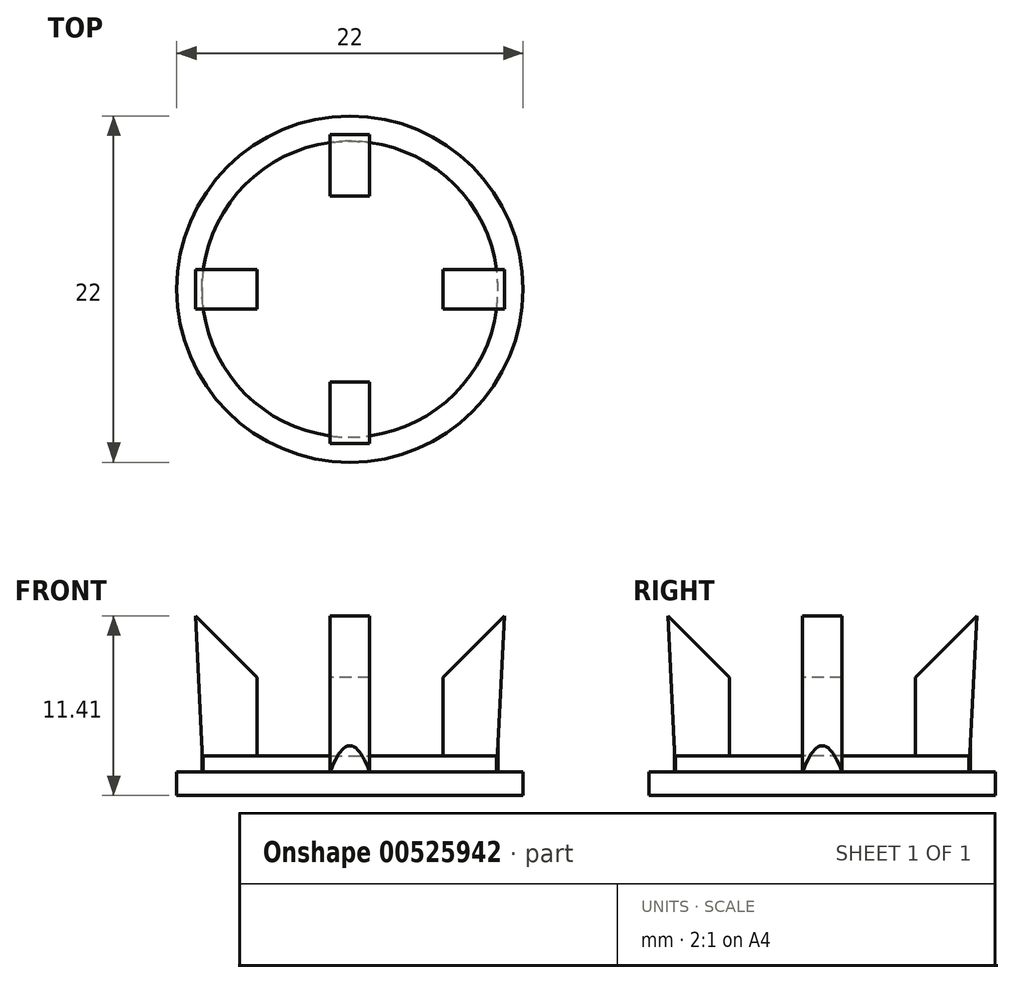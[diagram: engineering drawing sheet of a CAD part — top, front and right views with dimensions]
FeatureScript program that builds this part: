
annotation { "Feature Type Name" : "Feature", "Feature Type Description" : "" }
export const myFeature = defineFeature(function(context is Context, id is Id, definition is map)
    precondition{}
    {
        {
            var Q0;
            Q0=qCreatedBy(makeId("Top.planeOp"),FACE);
            var sketch = newSketch(context, id + "F0", { "sketchPlane" : qUnion([Q0])});
            skCircle(sketch, "E0", {"center": v(0, 0) * mm, "radius": 11 * mm});
            skCircle(sketch, "E1", {"center": v(0, 0) * mm, "radius": 9.4 * mm});
            skLineSegment(sketch, "E2.bottom", {"start": v(-12.9, 1.25) * mm, "end": v(-5.9, 1.25) * mm});
            skLineSegment(sketch, "E2.top", {"start": v(-12.9, -1.25) * mm, "end": v(-5.9, -1.25) * mm});
            skLineSegment(sketch, "E2.left", {"start": v(-12.9, 1.25) * mm, "end": v(-12.9, -1.25) * mm});
            skLineSegment(sketch, "E2.right", {"start": v(-5.9, 1.25) * mm, "end": v(-5.9, -1.25) * mm});
            skPoint(sketch, "E2.middle", {"position": v(-9.4, 0) * mm});
            skLineSegment(sketch, "E3.bottom", {"start": v(-1.25, 12.9) * mm, "end": v(1.25, 12.9) * mm});
            skLineSegment(sketch, "E3.top", {"start": v(-1.25, 5.9) * mm, "end": v(1.25, 5.9) * mm});
            skLineSegment(sketch, "E3.left", {"start": v(-1.25, 12.9) * mm, "end": v(-1.25, 5.9) * mm});
            skLineSegment(sketch, "E3.right", {"start": v(1.25, 12.9) * mm, "end": v(1.25, 5.9) * mm});
            skPoint(sketch, "E3.middle", {"position": v(0, 9.4) * mm});
            skLineSegment(sketch, "E4.bottom", {"start": v(12.9, 1.25) * mm, "end": v(5.9, 1.25) * mm});
            skLineSegment(sketch, "E4.top", {"start": v(12.9, -1.25) * mm, "end": v(5.9, -1.25) * mm});
            skLineSegment(sketch, "E4.left", {"start": v(12.9, 1.25) * mm, "end": v(12.9, -1.25) * mm});
            skLineSegment(sketch, "E4.right", {"start": v(5.9, 1.25) * mm, "end": v(5.9, -1.25) * mm});
            skPoint(sketch, "E4.middle", {"position": v(9.4, 0) * mm});
            skLineSegment(sketch, "E5.bottom", {"start": v(1.25, -5.9) * mm, "end": v(-1.25, -5.9) * mm});
            skLineSegment(sketch, "E5.top", {"start": v(1.25, -12.9) * mm, "end": v(-1.25, -12.9) * mm});
            skLineSegment(sketch, "E5.left", {"start": v(1.25, -5.9) * mm, "end": v(1.25, -12.9) * mm});
            skLineSegment(sketch, "E5.right", {"start": v(-1.25, -5.9) * mm, "end": v(-1.25, -12.9) * mm});
            skPoint(sketch, "E5.middle", {"position": v(0, -9.4) * mm});
            skSolve(sketch);
        }
        {
            var Q0;
            {var subQ0=sQuery(id+"F0.wireOp",EDGE,"E3.left");var subQ1=sQuery(id+"F0.wireOp",EDGE,"E0");var subQ2=makeQuery(id+"F0.imprint","INTERSECT",VERTEX,{"derivedFrom":[subQ1,subQ0]});Q0=makeQuery(id+"F0.imprint","IMPRINT",FACE,{"disambiguationData":[TD([[makeQuery(id+"F0.imprint","IMPRINT",EDGE,{"disambiguationData":[TD([[subQ2,-1.0]])],"derivedFrom":subQ1}),1.0]])]});}
            var Q1;
            {var subQ0=sQuery(id+"F0.wireOp",EDGE,"E2.top");var subQ1=sQuery(id+"F0.wireOp",EDGE,"E0");var subQ2=makeQuery(id+"F0.imprint","INTERSECT",VERTEX,{"derivedFrom":[subQ1,subQ0]});Q1=makeQuery(id+"F0.imprint","IMPRINT",FACE,{"disambiguationData":[TD([[makeQuery(id+"F0.imprint","IMPRINT",EDGE,{"disambiguationData":[TD([[subQ2,-1.0]])],"derivedFrom":subQ1}),1.0]])]});}
            var Q2;
            {var subQ0=sQuery(id+"F0.wireOp",EDGE,"E2.bottom");var subQ1=sQuery(id+"F0.wireOp",EDGE,"E0");var subQ2=makeQuery(id+"F0.imprint","INTERSECT",VERTEX,{"derivedFrom":[subQ1,subQ0]});Q2=makeQuery(id+"F0.imprint","IMPRINT",FACE,{"disambiguationData":[TD([[makeQuery(id+"F0.imprint","IMPRINT",EDGE,{"disambiguationData":[TD([[subQ2,-1.0]])],"derivedFrom":subQ1}),1.0]])]});}
            var Q3;
            {var subQ0=sQuery(id+"F0.wireOp",EDGE,"E5.left");var subQ1=sQuery(id+"F0.wireOp",EDGE,"E0");var subQ2=makeQuery(id+"F0.imprint","INTERSECT",VERTEX,{"derivedFrom":[subQ1,subQ0]});Q3=makeQuery(id+"F0.imprint","IMPRINT",FACE,{"disambiguationData":[TD([[makeQuery(id+"F0.imprint","IMPRINT",EDGE,{"disambiguationData":[TD([[subQ2,-1.0]])],"derivedFrom":subQ1}),1.0]])]});}
            var Q4;
            {var subQ0=sQuery(id+"F0.wireOp",EDGE,"E5.right");var subQ1=sQuery(id+"F0.wireOp",EDGE,"E0");var subQ2=makeQuery(id+"F0.imprint","INTERSECT",VERTEX,{"derivedFrom":[subQ1,subQ0]});Q4=makeQuery(id+"F0.imprint","IMPRINT",FACE,{"disambiguationData":[TD([[makeQuery(id+"F0.imprint","IMPRINT",EDGE,{"disambiguationData":[TD([[subQ2,-1.0]])],"derivedFrom":subQ1}),1.0]])]});}
            var Q5;
            {var subQ0=sQuery(id+"F0.wireOp",EDGE,"E3.right");var subQ1=sQuery(id+"F0.wireOp",EDGE,"E0");var subQ2=makeQuery(id+"F0.imprint","INTERSECT",VERTEX,{"derivedFrom":[subQ1,subQ0]});Q5=makeQuery(id+"F0.imprint","IMPRINT",FACE,{"disambiguationData":[TD([[makeQuery(id+"F0.imprint","IMPRINT",EDGE,{"disambiguationData":[TD([[subQ2,1.0]])],"derivedFrom":subQ1}),1.0]])]});}
            var Q6;
            {var subQ0=sQuery(id+"F0.wireOp",EDGE,"E4.bottom");var subQ1=sQuery(id+"F0.wireOp",EDGE,"E0");var subQ2=makeQuery(id+"F0.imprint","INTERSECT",VERTEX,{"derivedFrom":[subQ1,subQ0]});Q6=makeQuery(id+"F0.imprint","IMPRINT",FACE,{"disambiguationData":[TD([[makeQuery(id+"F0.imprint","IMPRINT",EDGE,{"disambiguationData":[TD([[subQ2,1.0]])],"derivedFrom":subQ1}),1.0]])]});}
            var Q7;
            {var subQ0=sQuery(id+"F0.wireOp",EDGE,"E3.right");var subQ1=sQuery(id+"F0.wireOp",EDGE,"E0");var subQ2=makeQuery(id+"F0.imprint","INTERSECT",VERTEX,{"derivedFrom":[subQ1,subQ0]});Q7=makeQuery(id+"F0.imprint","IMPRINT",FACE,{"disambiguationData":[TD([[makeQuery(id+"F0.imprint","IMPRINT",EDGE,{"disambiguationData":[TD([[subQ2,-1.0]])],"derivedFrom":subQ1}),1.0]])]});}
            var Q8;
            {var subQ8=sQuery(id+"F0.wireOp",EDGE,"E2.right");Q8=makeQuery(id+"F0.imprint","IMPRINT",FACE,{"disambiguationData":[TD([[makeQuery(id+"F0.imprint","IMPRINT",EDGE,{"derivedFrom":subQ8}),1.0]])]});}
            var Q9;
            {var subQ5=sQuery(id+"F0.wireOp",EDGE,"E3.top");Q9=makeQuery(id+"F0.imprint","IMPRINT",FACE,{"disambiguationData":[TD([[makeQuery(id+"F0.imprint","IMPRINT",EDGE,{"derivedFrom":subQ5}),1.0]])]});}
            var Q10;
            {var subQ5=sQuery(id+"F0.wireOp",EDGE,"E4.right");Q10=makeQuery(id+"F0.imprint","IMPRINT",FACE,{"disambiguationData":[TD([[makeQuery(id+"F0.imprint","IMPRINT",EDGE,{"derivedFrom":subQ5}),1.0]])]});}
            var Q11;
            {var subQ5=sQuery(id+"F0.wireOp",EDGE,"E2.right");Q11=makeQuery(id+"F0.imprint","IMPRINT",FACE,{"disambiguationData":[TD([[makeQuery(id+"F0.imprint","IMPRINT",EDGE,{"derivedFrom":subQ5}),-1.0]])]});}
            var Q12;
            {var subQ5=sQuery(id+"F0.wireOp",EDGE,"E5.bottom");Q12=makeQuery(id+"F0.imprint","IMPRINT",FACE,{"disambiguationData":[TD([[makeQuery(id+"F0.imprint","IMPRINT",EDGE,{"derivedFrom":subQ5}),1.0]])]});}
            extrude(context, id + "F1", {"entities" : qUnion([Q0, Q1, Q2, Q3, Q4, Q5, Q6, Q7, Q8, Q9, Q10, Q11, Q12]), "oppositeDirection" : true, "depth" : 1.5 * mm, "offsetDistance" : 25 * mm});
        }
        {
            var Q0;
            {var subQ5=sQuery(id+"F0.wireOp",EDGE,"E3.top");Q0=makeQuery(id+"F0.imprint","IMPRINT",FACE,{"disambiguationData":[TD([[makeQuery(id+"F0.imprint","IMPRINT",EDGE,{"derivedFrom":subQ5}),1.0]])]});}
            var Q1;
            {var subQ5=sQuery(id+"F0.wireOp",EDGE,"E4.right");Q1=makeQuery(id+"F0.imprint","IMPRINT",FACE,{"disambiguationData":[TD([[makeQuery(id+"F0.imprint","IMPRINT",EDGE,{"derivedFrom":subQ5}),1.0]])]});}
            var Q2;
            {var subQ5=sQuery(id+"F0.wireOp",EDGE,"E2.right");Q2=makeQuery(id+"F0.imprint","IMPRINT",FACE,{"disambiguationData":[TD([[makeQuery(id+"F0.imprint","IMPRINT",EDGE,{"derivedFrom":subQ5}),-1.0]])]});}
            var Q3;
            {var subQ5=sQuery(id+"F0.wireOp",EDGE,"E5.bottom");Q3=makeQuery(id+"F0.imprint","IMPRINT",FACE,{"disambiguationData":[TD([[makeQuery(id+"F0.imprint","IMPRINT",EDGE,{"derivedFrom":subQ5}),1.0]])]});}
            extrude(context, id + "F2", {"entities" : qUnion([Q0, Q1, Q2, Q3]), "operationType" : NewBodyOperationType.ADD, "depth" : 10 * mm, "offsetDistance" : 25 * mm});
        }
        {
            var Q0;
            Q0=makeQuery(id+"F2.opExtrude","SWEPT_FACE",FACE,{"disambiguationData":[OSD([sQuery(id+"F0.wireOp",EDGE,"E3.left")])]});
            var sketch = newSketch(context, id + "F3", { "sketchPlane" : qUnion([Q0])});
            skLineSegment(sketch, "E6", {"start": v(-9.32, 10) * mm, "end": v(-9.82, 10) * mm});
            skLineSegment(sketch, "E7", {"start": v(-9.82, 10) * mm, "end": v(-9.32, 0) * mm});
            skSolve(sketch);
        }
        {
            var Q0;
            Q0=makeQuery(id+"F3.imprint","IMPRINT",FACE,{"disambiguationData":[TD([[makeQuery(id+"F3.imprint","IMPRINT",EDGE,{"derivedFrom":sQuery(id+"F3.wireOp",EDGE,"E6")}),1.0]])]});
            extrude(context, id + "F4", {"entities" : qUnion([Q0]), "operationType" : NewBodyOperationType.ADD, "oppositeDirection" : true, "depth" : 2.5 * mm, "offsetDistance" : 25 * mm});
        }
        {
            var Q0;
            Q0=makeQuery(id+"F2.opExtrude","SWEPT_FACE",FACE,{"disambiguationData":[OSD([sQuery(id+"F0.wireOp",EDGE,"E5.right")])]});
            var sketch = newSketch(context, id + "F5", { "sketchPlane" : qUnion([Q0])});
            skLineSegment(sketch, "E8", {"start": v(9.32, 10) * mm, "end": v(9.82, 10) * mm});
            skLineSegment(sketch, "E9", {"start": v(9.82, 10) * mm, "end": v(9.32, 0) * mm});
            skSolve(sketch);
        }
        {
            var Q0;
            Q0=makeQuery(id+"F5.imprint","IMPRINT",FACE,{"disambiguationData":[TD([[makeQuery(id+"F5.imprint","IMPRINT",EDGE,{"derivedFrom":sQuery(id+"F5.wireOp",EDGE,"E8")}),-1.0]])]});
            extrude(context, id + "F6", {"entities" : qUnion([Q0]), "operationType" : NewBodyOperationType.ADD, "oppositeDirection" : true, "depth" : 2.5 * mm, "offsetDistance" : 25 * mm});
        }
        {
            var Q0;
            Q0=makeQuery(id+"F2.opExtrude","SWEPT_FACE",FACE,{"disambiguationData":[OSD([sQuery(id+"F0.wireOp",EDGE,"E2.top")])]});
            var sketch = newSketch(context, id + "F7", { "sketchPlane" : qUnion([Q0])});
            skLineSegment(sketch, "E10", {"start": v(-9.32, 10) * mm, "end": v(-9.82, 10) * mm});
            skLineSegment(sketch, "E11", {"start": v(-9.82, 10) * mm, "end": v(-9.32, 0) * mm});
            skSolve(sketch);
        }
        {
            var Q0;
            Q0=makeQuery(id+"F7.imprint","IMPRINT",FACE,{"disambiguationData":[TD([[makeQuery(id+"F7.imprint","IMPRINT",EDGE,{"derivedFrom":sQuery(id+"F7.wireOp",EDGE,"E10")}),1.0]])]});
            extrude(context, id + "F8", {"entities" : qUnion([Q0]), "operationType" : NewBodyOperationType.ADD, "oppositeDirection" : true, "depth" : 2.5 * mm, "offsetDistance" : 25 * mm});
        }
        {
            var Q0;
            Q0=makeQuery(id+"F2.opExtrude","SWEPT_FACE",FACE,{"disambiguationData":[OSD([sQuery(id+"F0.wireOp",EDGE,"E4.top")])]});
            var sketch = newSketch(context, id + "F9", { "sketchPlane" : qUnion([Q0])});
            skLineSegment(sketch, "E12", {"start": v(9.32, 10) * mm, "end": v(9.82, 10) * mm});
            skLineSegment(sketch, "E13", {"start": v(9.82, 10) * mm, "end": v(9.32, 0) * mm});
            skSolve(sketch);
        }
        {
            var Q0;
            Q0=makeQuery(id+"F9.imprint","IMPRINT",FACE,{"disambiguationData":[TD([[makeQuery(id+"F9.imprint","IMPRINT",EDGE,{"derivedFrom":sQuery(id+"F9.wireOp",EDGE,"E12")}),-1.0]])]});
            extrude(context, id + "F10", {"entities" : qUnion([Q0]), "operationType" : NewBodyOperationType.ADD, "oppositeDirection" : true, "depth" : 2.5 * mm, "offsetDistance" : 25 * mm});
        }
        {
            var Q0;
            {var subQ8=sQuery(id+"F0.wireOp",EDGE,"E2.right");Q0=makeQuery(id+"F0.imprint","IMPRINT",FACE,{"disambiguationData":[TD([[makeQuery(id+"F0.imprint","IMPRINT",EDGE,{"derivedFrom":subQ8}),1.0]])]});}
            extrude(context, id + "F11", {"entities" : qUnion([Q0]), "operationType" : NewBodyOperationType.ADD, "depth" : 1 * mm, "offsetDistance" : 25 * mm});
        }
        {
            var Q0;
            Q0=makeQuery(id+"F2.opExtrude","CAP_EDGE",EDGE,{"disambiguationData":[OSD([sQuery(id+"F0.wireOp",EDGE,"E3.top")])],"isStart":false});
            var Q1;
            Q1=makeQuery(id+"F2.opExtrude","CAP_EDGE",EDGE,{"disambiguationData":[OSD([sQuery(id+"F0.wireOp",EDGE,"E4.right")])],"isStart":false});
            var Q2;
            Q2=makeQuery(id+"F2.opExtrude","CAP_EDGE",EDGE,{"disambiguationData":[OSD([sQuery(id+"F0.wireOp",EDGE,"E2.right")])],"isStart":false});
            var Q3;
            Q3=makeQuery(id+"F2.opExtrude","CAP_EDGE",EDGE,{"disambiguationData":[OSD([sQuery(id+"F0.wireOp",EDGE,"E5.bottom")])],"isStart":false});
            chamfer(context, id + "F12", {"entities" : qUnion([Q0, Q1, Q2, Q3]), "width" : 4 * mm, "tangentPropagation" : true});
        }
    });
